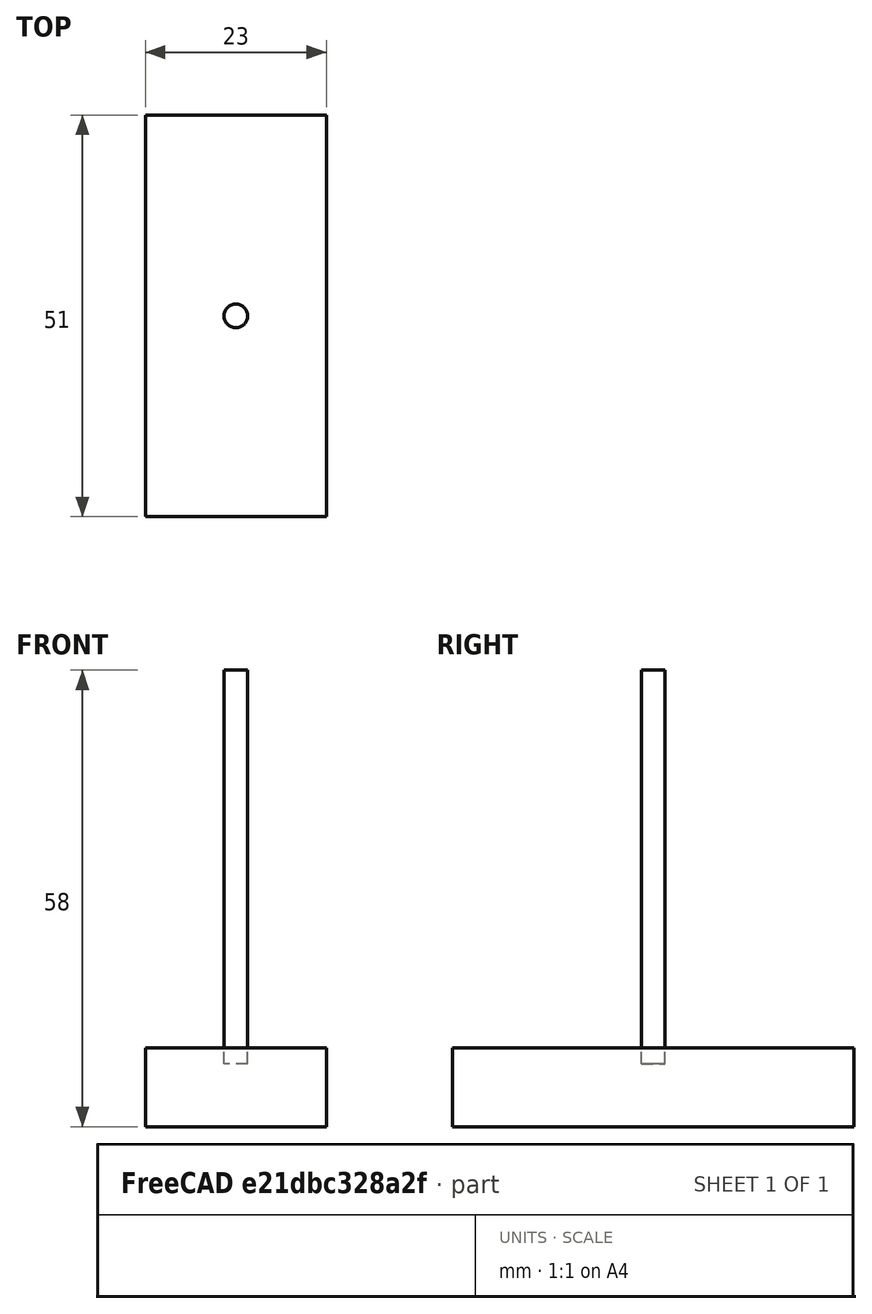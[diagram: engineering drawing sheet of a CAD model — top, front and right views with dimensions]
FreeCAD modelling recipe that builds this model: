
FCSTD DOCUMENT  (FreeCAD 1.0R39109 (Git))
Label: LatchFastening
License: All rights reserved
LicenseURL: http://en.wikipedia.org/wiki/All_rights_reserved
objects: Path::FeaturePython×6, Part::FeaturePython×3, App::DocumentObjectGroup×3, Part::Feature×1, App::FeaturePython×1
note: 7 computed .brp shape members not serialized (recipe doc carries the construction recipe); baked Part::Feature solids carry a one-line shape summary decoded from their .brp

FEATURE [Part::Feature] Solid  label="LatchFasteningSTEP"
  shape: bbox 15 x 43 x 8 mm, 24 faces (baked)
FEATURE [App::FeaturePython] SetupSheet  # Path/CAM operation (typed FeaturePython)
  ClearanceHeightExpression = OpStockZMax+SetupSheet.ClearanceHeightOffset
  ClearanceHeightOffset = 5
  CoolantMode = 0
  CoolantModes = None | Flood | Mist
  FinalDepthExpression = OpFinalDepth
  HorizRapid = 0
  SafeHeightExpression = OpStockZMax+SetupSheet.SafeHeightOffset
  SafeHeightOffset = 3
  StartDepthExpression = OpStartDepth
  StepDownExpression = OpToolDiameter
  VertRapid = 0
FEATURE [Part::FeaturePython] Clone  label="Model-LatchFasteningSTEP"  # Draft clone (typed FeaturePython)
  AttacherType = Attacher::AttachEngine3D
  Fuse = false
  Objects = -> [Solid]
  PathResource = Model
  Placement = pos=(7.5,21.5,-9e-16) rot=(0,-1,0;3.14159rad)
  Scale = (1,1,1)
FEATURE [App::DocumentObjectGroup] Model
  Group = -> [Clone]
FEATURE [Part::FeaturePython] Stock  # WARN: FeaturePython — macro-defined, semantics opaque (R4)
  Base = -> Model
  ExtXneg = 4
  ExtXpos = 4
  ExtYneg = 4
  ExtYpos = 4
  ExtZneg = 0
  ExtZpos = 2
  Placement = pos=(-7.5,-21.5,-8) rot=(0,0,1;0rad)
  StockType = FromBase
FEATURE [Part::FeaturePython] ToolBit001  label="3mm Endmill"  # Path/CAM toolbit (typed FeaturePython)
  BitPropertyNames = Chipload | CuttingEdgeHeight | Diameter | Flutes | Length | Material | ShankDiameter | SpindleDirection
  BitShape = <path>
  Chipload = 0
  CuttingEdgeHeight = 15
  Diameter = 3
  File = <path>
  Flutes = 0
  Length = 50
  Material = 0
  ShankDiameter = 3
  ShapeName = endmill
  SpindleDirection = 0
FEATURE [Path::FeaturePython] _mm_Endmill  label="3mm Endmill001"  # Path/CAM operation (typed FeaturePython)
  HorizFeed = 6.66667
  HorizRapid = 0
  SpindleDir = 0
  SpindleSpeed = 10000
  Tool = -> ToolBit001
  ToolNumber = 2
  VertFeed = 6.66667
  VertRapid = 0
  expr: HorizRapid = SetupSheet.HorizRapid
  expr: VertRapid = SetupSheet.VertRapid
FEATURE [App::DocumentObjectGroup] Tools
  Group = -> [_mm_Endmill]
FEATURE [Path::FeaturePython] Adaptive  # Path/CAM operation (typed FeaturePython)
  Active = true
  Base = -> [Clone]
  ClearanceHeight = 7
  CoolantMode = 0
  CycleTime = 00:01:57
  ExtensionCorners = true
  ExtensionLengthDefault = 1.5
  FinalDepth = -6
  FinishDepth = 0
  FinishingProfile = true
  ForceInsideOut = false
  HelixAngle = 5
  HelixConeAngle = 0
  HelixDiameterLimit = 1.5
  KeepToolDownRatio = 3
  LiftDistance = 0
  OpFinalDepth = -6
  OpStartDepth = 2
  OpStockZMax = 2
  OpStockZMin = -8
  OpToolDiameter = 3
  OperationType = 0
  SafeHeight = 5
  Side = 1
  StartDepth = 2
  StepDown = 6
  StepOver = 10
  StockToLeave = 0
  StopProcessing = false
  Stopped = false
  Tolerance = 0.1
  ToolController = -> _mm_Endmill
  UseHelixArcs = false
  UseOutline = false
  expr: ClearanceHeight = OpStockZMax + SetupSheet.ClearanceHeightOffset
  expr: ExtensionLengthDefault = OpToolDiameter / 2
  expr: FinalDepth = OpFinalDepth
  expr: SafeHeight = OpStockZMax + SetupSheet.SafeHeightOffset
  expr: StartDepth = OpStartDepth
  expr: StepDown = OpToolDiameter * 2
FEATURE [Path::FeaturePython] Helix  # Path/CAM operation (typed FeaturePython)
  Active = true
  Base = -> [Clone]
  ClearanceHeight = 7
  CoolantMode = 0
  CutMode = 0
  CycleTime = 00:00:14
  Direction = 1
  Disabled = Clone.Edge46 | Clone.Edge45
  FinalDepth = -8
  OffsetExtra = 0
  OpFinalDepth = -8
  OpStartDepth = 2
  OpStockZMax = 2
  OpStockZMin = -8
  OpToolDiameter = 3
  SafeHeight = 5
  StartDepth = -6
  StartRadius = 0
  StartSide = 1
  StepDown = 0.375
  StepOver = 50
  ToolController = -> _mm_Endmill
  expr: ClearanceHeight = OpStockZMax + SetupSheet.ClearanceHeightOffset
  expr: FinalDepth = OpFinalDepth
  expr: SafeHeight = OpStockZMax + SetupSheet.SafeHeightOffset
  expr: StepDown = OpToolDiameter / 8
FEATURE [Path::FeaturePython] Adaptive001  label="OutCut"  # Path/CAM operation (typed FeaturePython)
  Active = true
  Base = -> [Clone]
  ClearanceHeight = 7
  CoolantMode = 0
  CycleTime = 00:17:46
  ExtensionCorners = true
  ExtensionLengthDefault = 1.5
  FinalDepth = -8
  FinishDepth = 0
  FinishingProfile = true
  ForceInsideOut = false
  HelixAngle = 5
  HelixConeAngle = 0
  HelixDiameterLimit = 1
  KeepToolDownRatio = 3
  LiftDistance = 0
  OpFinalDepth = -8
  OpStartDepth = 2
  OpStockZMax = 2
  OpStockZMin = -8
  OpToolDiameter = 3
  OperationType = 1
  SafeHeight = 5
  Side = 0
  StartDepth = 0
  StepDown = 4.5
  StepOver = 10
  StockToLeave = 0
  StopProcessing = false
  Stopped = false
  Tolerance = 0.1
  ToolController = -> _mm_Endmill
  UseHelixArcs = false
  UseOutline = false
  expr: ClearanceHeight = OpStockZMax + SetupSheet.ClearanceHeightOffset
  expr: ExtensionLengthDefault = OpToolDiameter / 2
  expr: FinalDepth = OpFinalDepth
  expr: SafeHeight = OpStockZMax + SetupSheet.SafeHeightOffset
  expr: StepDown = OpToolDiameter * 1.5
FEATURE [Path::FeaturePython] MillFace  # Path/CAM operation (typed FeaturePython)
  Active = true
  AreaParams:
    Tolerance = 1e-07
    FitArcs = True
    Simplify = False
    CleanDistance = 0.0
    Accuracy = 0.01
    Unit = 1.0
    MinArcPoints = 4
    MaxArcPoints = 100
    ClipperScale = 10000000.0
    Fill = 0
    Coplanar = 0
    Reorient = True
    Outline = False
    Explode = False
    OpenMode = 0
    Deflection = 0.01
    SubjectFill = 0
    ClipFill = 0
    Offset = 0.0
    ExtraPass = 0
    Stepover = 0.0
    LastStepover = 0.0
    JoinType = 0
    EndType = 0
    MiterLimit = 2.0
    RoundPrecision = 0.0
    PocketMode = 1
    ToolRadius = 1.5
    PocketExtraOffset = 0.0
    PocketStepover = 0.75
    PocketLastStepover = 0.0
    FromCenter = True
    Angle = 45.0
    AngleShift = 0.0
    Shift = 0.0
    Thicken = False
    SectionCount = -1
    Stepdown = 1.0
    SectionOffset = 0.0
    SectionTolerance = 1e-06
    SectionMode = 2
    Project = False
  Base = -> [Clone]
  BoundaryShape = 3
  ClearEdges = true
  ClearanceHeight = 7
  CoolantMode = 0
  CutMode = 0
  CycleTime = 00:03:29
  ExcludeRaisedAreas = false
  ExtraOffset = 0
  FinalDepth = -1e-15
  FinishDepth = 0
  KeepToolDown = false
  MinTravel = false
  OffsetPattern = 0
  OpFinalDepth = -1e-15
  OpStartDepth = 2
  OpStockZMax = 2
  OpStockZMin = -8
  OpToolDiameter = 3
  PathParams = {'orientation': 1, 'feedrate': 6.666666666666667, 'feedrate_v': 6.666666666666667, 'verbose': True, 'resume_height': 5.0, 'retraction': 7.0, 'return_end': True, 'preamble': False}
  PocketLastStepOver = 0
  SafeHeight = 5
  SplitArcs = false
  StartAt = 0
  StartDepth = 2
  StartPoint = (0,0,0)
  StepDown = 3
  StepOver = 25
  ToolController = -> _mm_Endmill
  UseRestMachining = false
  UseStartPoint = false
  ZigZagAngle = 45
  expr: ClearanceHeight = OpStockZMax + SetupSheet.ClearanceHeightOffset
  expr: FinalDepth = OpFinalDepth
  expr: SafeHeight = OpStockZMax + SetupSheet.SafeHeightOffset
  expr: StartDepth = OpStartDepth
  expr: StepDown = OpToolDiameter
FEATURE [App::DocumentObjectGroup] Operations
  Group = -> [MillFace,Adaptive,Helix,Adaptive001]
FEATURE [Path::FeaturePython] Job  label="CutCountur"  # Path/CAM operation (typed FeaturePython)
  CycleTime = 00:23:26
  Fixtures = G54
  GeometryTolerance = 0.01
  JobType = 0
  Model = -> Model
  Operations = -> Operations
  OrderOutputBy = 0
  PostProcessor = 11
  PostProcessorArgs = --bcnc
  PostProcessorOutputFile = %D\%d
  SetupSheet = -> SetupSheet
  SplitOutput = false
  Stock = -> Stock
  Tools = -> Tools
note: 2 file-system paths scrubbed to <path> (originals preserved in the JSON sidecar)
